# Revit family: LEGRAND_TOMAS SIN ENCLAVAMIENTO_DE SUPERFICIE_IP66_500
name_source: partatom
category: Installations électriques
revit_build: Autodesk Revit 2018 (Build: 20170223_1515(x64)
units: mm (PartAtom-declared; Revit-internal decimal feet)

## family parameters
Conserver l'orientation des annotations = Non
Cote de connecteur circulaire = Utiliser le diamètre
Couper avec des vides une fois chargée = Non
Hôte = Face
Partagée = Non
Point de calcul de pièce = Non
Type d'élément = Normal

## types (1)
- base para cuadro Hypra  IP 66/67-55   63A   500 V   3P+T   plast caja de superficie para cableado de paso
    Condiciones Generales de Uso = https://export.legrand.com
    Description = Toma AL estándar internacional para montaje empotrado o en superficie con accesorio permite la alimentación de aparatos de potencia
    Dia bouchon = 90 mm  [stored 0.295276 ft]
    Elévation par défaut = 1000 mm  [stored 3.28084 ft]
    Estándar CEI o NFC = CEI
    Fabricant = Legrand
    L2 = 45 mm  [stored 0.147638 ft]
    Modèle = 059429
    RAY BOUCHON = 45 mm  [stored 0.147638 ft]
    Ray = 30 mm  [stored 0.0984252 ft]
    Temperatura maxima de instalación = 40°C
    Temperatura maxima de uso = 100°C
    Temperatura minima de instalación = -20°C
    Temperatura minima de uso = -50°C
    Tension V = 500 V  50/60 Hz negro
    altura mm = 300 mm
    ancho mm = 170 mm  [stored 0.557743 ft]
    clase de protección IP = IP66/67-55
    color característico = negro
    dIA = 60 mm  [stored 0.19685 ft]
    distancia de fijación horizontal mm = 77 mm
    distancia de fijación vertical mm = 85 mm  [stored 0.278871 ft]
    h1 = 180 mm  [stored 0.590551 ft]
    instalación de empotrar E o de superficie S = empotrar y superficie
    intensidad A = 63 A
    materia de la caja = plástico
    numero de polos = 4
    posición de la tierra h = 7
    profundidad de empotrar mm = 150 mm
    profundidad mm = 255 mm  [stored 0.836614 ft]
    resistencia a los choques IK = 09
    sin halogeno = Non
    tipo de conexión = conexión por tonillo

note: [stored X ft] marks values corroborated as IEEE doubles in the binary element streams (Revit-internal decimal feet)
